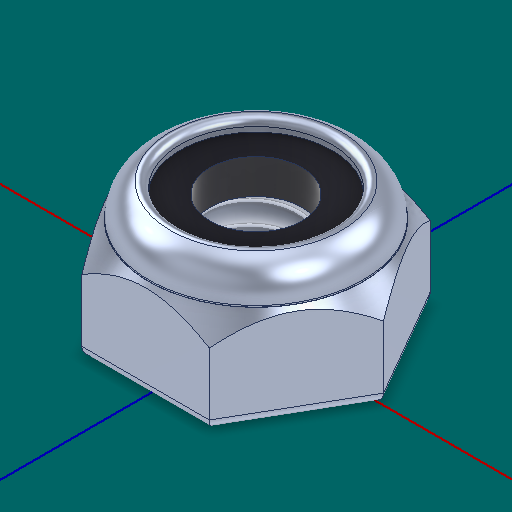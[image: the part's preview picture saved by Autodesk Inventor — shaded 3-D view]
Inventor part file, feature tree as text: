
AUTODESK INVENTOR PART (.ipt)
format: ipt  version: 2025 (Build 290162000, 162)  size: 233,472 bytes
history: native  units: in
note: dims shown in document units (in); Inventor stores cm internally (conversion verified against a paired STEP export)
features: other x4, sketch x2, plane x1
ambient origin geometry x8: Origin, YZ Plane, XZ Plane, XY Plane, X Axis, Y Axis, Z Axis, Center Point
bodies: Body1 (feature_tree)
feature tree (7):
  other  "Nut Thin Nylock_mirrored.ipt"
  other  "NONE::Nut Thin Nylock_mirrored.ipt"
  other  "TaggingFeature1"
  sketch  "Sketch1"  dims[d0=0.3937in]
  sketch  "Sketch2"
  plane  "Work Plane1"
  parser-record x1  (decoder bookkeeping rows leaked as tree rows — omitted from the tree; the rows remain in map.json)
